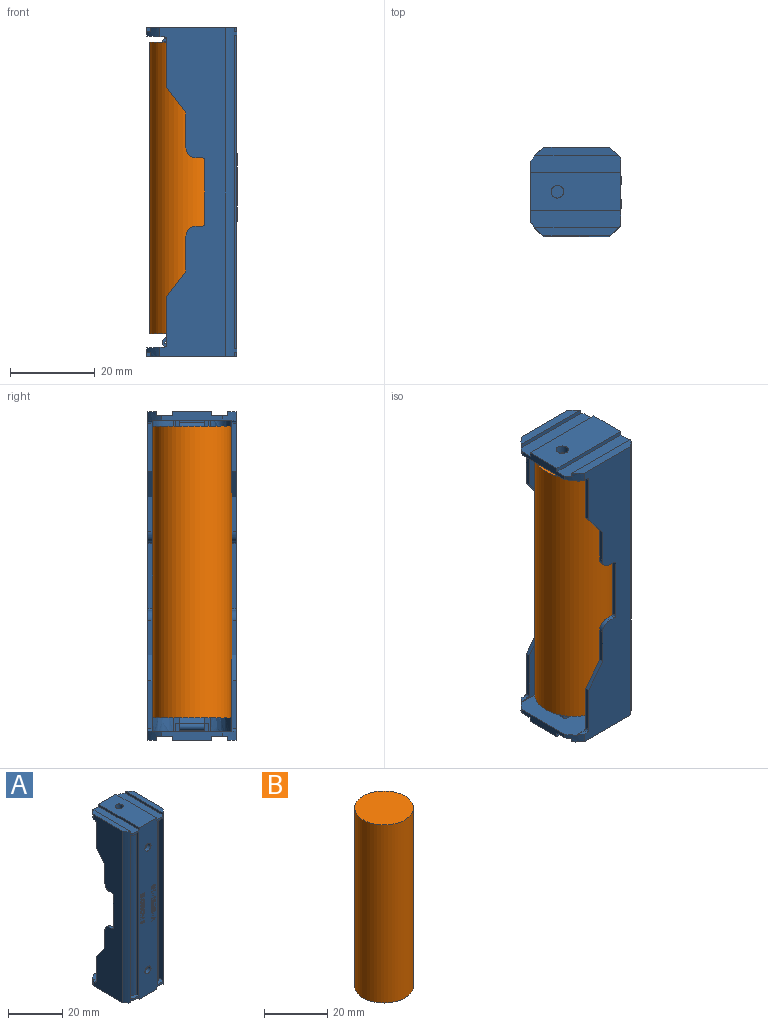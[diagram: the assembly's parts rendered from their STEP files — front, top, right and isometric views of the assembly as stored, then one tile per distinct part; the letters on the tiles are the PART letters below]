
ASSEMBLY  parts=2 mates=1
PART A: 400 faces, bbox 22.9x23.4x83.1 mm
  f0: plane 77.7x15.49mm, normal (0,-1,0), area 740.8mm2, adj f18,f19,f22,f24,f26,f27,f29,f30
  f1: plane 14.29x2mm, normal (0,1,0), area 23.3mm2, adj f5,f22,f24,f32,f120,f121,f396,f397
  f2: plane 19.76x2mm, normal (0,0,-1), area 35.5mm2, adj f9,f23,f394,f396
  f3: plane 19.76x2mm, normal (0,0,-1), area 35.5mm2, adj f10,f21,f395,f397
  f4: plane 19.3x18.9mm, normal (0,0,-1), area 320.5mm2, adj f6,f8,f11,f31,f35,f72,f73,f107
  f5: plane 19.3x18.9mm, normal (0,0,1), area 320.5mm2, adj f1,f7,f12,f31,f38,f72,f73,f96
  f6: plane 28.81x10.37mm, normal (1,0,0), area 156.1mm2, adj f4,f13,f42,f43,f44,f45,f46,f47
  f7: plane 28.81x10.37mm, normal (-1,0,0), area 156.1mm2, adj f5,f15,f57,f58,f59,f60,f61,f62
  f8: plane 14.29x2mm, normal (0,1,0), area 23.3mm2, adj f4,f18,f19,f33,f117,f118,f398,f399
  f9: plane 77.7x15.47mm, normal (1,0,0), area 815.6mm2, adj f2,f15,f16,f41,f57,f58,f59,f60
  f10: plane 77.7x15.47mm, normal (-1,0,0), area 815.6mm2, adj f3,f13,f14,f34,f42,f43,f44,f45
  f11: plane 28.81x10.37mm, normal (-1,0,0), area 156.1mm2, adj f4,f16,f66,f67,f68,f69,f70,f71
  f12: plane 28.81x10.37mm, normal (1,0,0), area 156.1mm2, adj f5,f14,f51,f52,f53,f54,f55,f56
  f13: plane 2.19x1mm, normal (0,0,-1), area 1.6mm2, adj f6,f10,f42,f399
  f14: plane 2.19x1mm, normal (0,0,1), area 1.6mm2, adj f10,f12,f56,f397
  f15: plane 2.19x1mm, normal (0,0,1), area 1.6mm2, adj f7,f9,f57,f396
  f16: plane 2.19x1mm, normal (0,0,-1), area 1.6mm2, adj f9,f11,f71,f398
  f17: plane 19.76x1mm, normal (1,0,0), area 19.8mm2, adj f18,f34,f395,f399
  f18: plane 21.3x3.95mm, normal (0,0,1), area 83.3mm2, adj f0,f8,f17,f117,f395,f399
  f19: plane 21.3x3.95mm, normal (0,0,1), area 83.3mm2, adj f0,f8,f20,f118,f394,f398
  f20: plane 19.76x1mm, normal (-1,0,0), area 19.8mm2, adj f19,f41,f394,f398
  f21: plane 19.76x1mm, normal (1,0,0), area 19.8mm2, adj f3,f22,f395,f397
  f22: plane 21.3x3.95mm, normal (0,0,-1), area 83.3mm2, adj f0,f1,f21,f120,f395,f397
  f23: plane 19.76x1mm, normal (-1,0,0), area 19.8mm2, adj f2,f24,f394,f396
  f24: plane 21.3x3.95mm, normal (0,0,-1), area 83.3mm2, adj f0,f1,f23,f121,f394,f396
  f25: plane 74x2.46mm, normal (1,0,0), area 181.8mm2, adj f26,f27,f123,f395
  f26: plane 3.72x3.24mm, normal (0,0,-1), area 5.8mm2, adj f0,f25,f122,f123,f395
  f27: plane 3.71x3.23mm, normal (0,0,1), area 5.8mm2, adj f0,f25,f122,f123,f395
  f28: plane 74x2.46mm, normal (-1,0,0), area 181.8mm2, adj f29,f30,f125,f394
  f29: plane 3.72x3.24mm, normal (0,0,-1), area 5.8mm2, adj f0,f28,f124,f125,f394
  f30: plane 3.71x3.23mm, normal (0,0,1), area 5.8mm2, adj f0,f28,f124,f125,f394
  f31: plane 73.7x8.9mm, normal (0,1,0), area 572.8mm2, adj f4,f5,f36,f39,f72,f73,f97,f98
  f32: plane 21.3x9mm, normal (0,0,-1), area 184.6mm2, adj f0,f1,f119,f120,f121
  f33: plane 21.3x9mm, normal (0,0,1), area 184.6mm2, adj f0,f8,f116,f117,f118
  f34: plane 19.76x2mm, normal (0,0,1), area 35.5mm2, adj f10,f17,f395,f399
  f35: plane 6x0.58mm, normal (0,1,0), area 3.4mm2, adj f4,f74,f107,f112
  f36: plane 14.74x6mm, normal (0,0,-1), area 79.4mm2, adj f31,f37,f75,f76,f106,f108,f111,f113
  f37: plane 9.57x5.89mm, normal (-1,0,0), area 10.8mm2, adj f36,f74,f76,f77,f78,f79,f80,f81
  f38: plane 6x0.34mm, normal (0,1,0), area 2mm2, adj f5,f85,f96,f101
  f39: plane 14.74x6mm, normal (0,0,1), area 79.4mm2, adj f31,f40,f86,f95,f99,f100,f104,f105
  f40: plane 9.57x5.89mm, normal (1,0,0), area 10.8mm2, adj f39,f85,f87,f88,f89,f90,f91,f92
  f41: plane 19.76x2mm, normal (0,0,1), area 35.5mm2, adj f9,f20,f394,f398
  f42: cylinder r=0.56mm len=1mm, axis (1,0,0), area 0.9mm2, adj f6,f10,f13,f43
  f43: plane 11.35x1mm, normal (0,1,0), area 11.4mm2, adj f6,f10,f42,f44
  f44: plane 6.08x4.59mm, normal (0,0.8,-0.6), area 7.6mm2, adj f6,f10,f43,f45
  f45: plane 8.25x1mm, normal (0,1,0), area 8.2mm2, adj f6,f10,f44,f46
  f46: cylinder r=2.38mm len=2.38mm, axis (1,0,0), area 3.7mm2, adj f6,f10,f45,f47
  f47: plane 1.56x1.05mm, normal (0,0,-1), area 1.6mm2, adj f6,f10,f46,f48,f73
  f48: cylinder r=0.46mm len=1.1mm, axis (1,0,0), area 0.8mm2, adj f10,f47,f49,f73
  f49: plane 15.17x1.1mm, normal (0,1,0), area 16.6mm2, adj f10,f48,f50,f73
  f50: cylinder r=0.46mm len=1.1mm, axis (1,0,0), area 0.8mm2, adj f10,f49,f51,f73
  f51: plane 1.56x1.05mm, normal (0,0,1), area 1.6mm2, adj f10,f12,f50,f52,f73
  f52: cylinder r=2.38mm len=2.38mm, axis (1,0,0), area 3.7mm2, adj f10,f12,f51,f53
  f53: plane 8.25x1mm, normal (0,1,0), area 8.2mm2, adj f10,f12,f52,f54
  f54: plane 6.08x4.59mm, normal (0,0.8,0.6), area 7.6mm2, adj f10,f12,f53,f55
  f55: plane 11.35x1mm, normal (0,1,0), area 11.4mm2, adj f10,f12,f54,f56
  f56: cylinder r=0.56mm len=1mm, axis (1,0,0), area 0.9mm2, adj f10,f12,f14,f55
  f57: cylinder r=0.56mm len=1mm, axis (1,0,0), area 0.9mm2, adj f7,f9,f15,f58
  f58: plane 11.35x1mm, normal (0,1,0), area 11.4mm2, adj f7,f9,f57,f59
  f59: plane 6.08x4.59mm, normal (0,0.8,0.6), area 7.6mm2, adj f7,f9,f58,f60
  f60: plane 8.25x1mm, normal (0,1,0), area 8.2mm2, adj f7,f9,f59,f61
  f61: cylinder r=2.38mm len=2.38mm, axis (1,0,0), area 3.7mm2, adj f7,f9,f60,f62
  f62: plane 1.56x1.05mm, normal (0,0,1), area 1.6mm2, adj f7,f9,f61,f63,f72
  f63: cylinder r=0.46mm len=1.1mm, axis (1,0,0), area 0.8mm2, adj f9,f62,f64,f72
  f64: plane 15.17x1.1mm, normal (0,1,0), area 16.6mm2, adj f9,f63,f65,f72
  f65: cylinder r=0.46mm len=1.1mm, axis (1,0,0), area 0.8mm2, adj f9,f64,f66,f72
  f66: plane 1.56x1.05mm, normal (0,0,-1), area 1.6mm2, adj f9,f11,f65,f67,f72
  f67: cylinder r=2.38mm len=2.38mm, axis (1,0,0), area 3.7mm2, adj f9,f11,f66,f68
  f68: plane 8.25x1mm, normal (0,1,0), area 8.2mm2, adj f9,f11,f67,f69
  f69: plane 6.08x4.59mm, normal (0,0.8,-0.6), area 7.6mm2, adj f9,f11,f68,f70
  f70: plane 11.35x1mm, normal (0,1,0), area 11.4mm2, adj f9,f11,f69,f71
  f71: cylinder r=0.56mm len=1mm, axis (1,0,0), area 0.9mm2, adj f9,f11,f16,f70
  f72: extruded ~73.7x7mm, area 677.7mm2, adj f4,f5,f7,f11,f31,f62,f63,f64
  f73: extruded ~73.7x7mm, area 677.7mm2, adj f4,f5,f6,f12,f31,f47,f48,f49
  f74: plane 14.74x6mm, normal (0,0,1), area 88.4mm2, adj f35,f37,f75,f84,f107,f112
  f75: plane 9.57x5.89mm, normal (1,0,0), area 10.8mm2, adj f36,f74,f76,f77,f78,f79,f80,f81
  f76: cylinder r=0.31mm len=6mm, axis (-1,0,0), area 4.3mm2, adj f36,f37,f75,f77
  f77: plane 6x3.97mm, normal (0,-0.71,0.7), area 33.5mm2, adj f37,f75,f76,f78
  f78: cylinder r=0.67mm len=6mm, axis (-1,0,0), area 3.2mm2, adj f37,f75,f77,f79
  f79: plane 6x4.49mm, normal (0,0,1), area 26.9mm2, adj f37,f75,f78,f80
  f80: plane 6x0.6mm, normal (0,-1,0), area 3.6mm2, adj f37,f75,f79,f81
  f81: plane 6x4.49mm, normal (0,0,-1), area 26.9mm2, adj f37,f75,f80,f82
  f82: cylinder r=1.27mm len=6mm, axis (-1,0,0), area 6mm2, adj f37,f75,f81,f83
  f83: plane 6x3.97mm, normal (0,0.71,-0.7), area 33.5mm2, adj f37,f75,f82,f84
  f84: cylinder r=0.91mm len=6mm, axis (-1,0,0), area 12.8mm2, adj f37,f74,f75,f83
  f85: plane 14.74x6mm, normal (0,0,-1), area 88.4mm2, adj f38,f40,f86,f87,f96,f101
  f86: plane 9.57x5.89mm, normal (-1,0,0), area 10.8mm2, adj f39,f85,f87,f88,f89,f90,f91,f92
  f87: cylinder r=0.91mm len=6mm, axis (-1,0,0), area 12.8mm2, adj f40,f85,f86,f88
  f88: plane 6x3.97mm, normal (0,0.71,0.7), area 33.5mm2, adj f40,f86,f87,f89
  f89: cylinder r=1.27mm len=6mm, axis (-1,0,0), area 6mm2, adj f40,f86,f88,f90
  f90: plane 6x4.49mm, normal (0,0,1), area 26.9mm2, adj f40,f86,f89,f91
  f91: plane 6x0.6mm, normal (0,-1,0), area 3.6mm2, adj f40,f86,f90,f92
  f92: plane 6x4.49mm, normal (0,0,-1), area 26.9mm2, adj f40,f86,f91,f93
  f93: cylinder r=0.67mm len=6mm, axis (-1,0,0), area 3.2mm2, adj f40,f86,f92,f94
  f94: plane 6x3.97mm, normal (0,-0.71,-0.7), area 33.5mm2, adj f40,f86,f93,f95
  f95: cylinder r=0.31mm len=6mm, axis (-1,0,0), area 4.3mm2, adj f39,f40,f86,f94
  f96: plane 9x0.34mm, normal (1,0,0), area 3.1mm2, adj f5,f38,f85,f100
  f97: plane 9x1.94mm, normal (-1,0,0), area 17.5mm2, adj f5,f31,f98,f100
  f98: plane 9x1.5mm, normal (0,0,1), area 13.5mm2, adj f31,f97,f99,f100
  f99: plane 9x1mm, normal (1,0,0), area 9mm2, adj f31,f39,f98,f100
  f100: plane 1.94x1.5mm, normal (0,1,0), area 2.4mm2, adj f5,f39,f86,f96,f97,f98,f99
  f101: plane 9x0.34mm, normal (-1,0,0), area 3.1mm2, adj f5,f38,f85,f105
  f102: plane 9x1.5mm, normal (0,0,1), area 13.5mm2, adj f31,f103,f104,f105
  f103: plane 9x1.94mm, normal (1,0,0), area 17.5mm2, adj f5,f31,f102,f105
  f104: plane 9x1mm, normal (-1,0,0), area 9mm2, adj f31,f39,f102,f105
  f105: plane 1.94x1.5mm, normal (0,1,0), area 2.4mm2, adj f5,f39,f40,f101,f102,f103,f104
  f106: plane 9x0.76mm, normal (-1,0,0), area 6.9mm2, adj f31,f36,f108,f110
  f107: plane 9x0.58mm, normal (-1,0,0), area 5.2mm2, adj f4,f35,f74,f108
  f108: plane 1.94x1.5mm, normal (0,1,0), area 2.3mm2, adj f4,f36,f75,f106,f107,f109,f110
  f109: plane 9x1.94mm, normal (1,0,0), area 17.5mm2, adj f4,f31,f108,f110
  f110: plane 9x1.5mm, normal (0,0,-1), area 13.5mm2, adj f31,f106,f108,f109
  f111: plane 9x0.76mm, normal (1,0,0), area 6.9mm2, adj f31,f36,f113,f114
  f112: plane 9x0.58mm, normal (1,0,0), area 5.2mm2, adj f4,f35,f74,f113
  f113: plane 1.94x1.5mm, normal (0,1,0), area 2.3mm2, adj f4,f36,f37,f111,f112,f114,f115
  f114: plane 9x1.5mm, normal (0,0,-1), area 13.5mm2, adj f31,f111,f113,f115
  f115: plane 9x1.94mm, normal (-1,0,0), area 17.5mm2, adj f4,f31,f113,f114
  f116: cylinder r=1.5mm len=3mm, axis (0,0,1), area 18.8mm2, adj f4,f33
  f117: plane 21.3x1mm, normal (-1,0,0), area 21.3mm2, adj f0,f8,f18,f33
  f118: plane 21.3x1mm, normal (1,0,0), area 21.3mm2, adj f0,f8,f19,f33
  f119: cylinder r=1.5mm len=3mm, axis (0,0,-1), area 18.8mm2, adj f5,f32
  f120: plane 21.3x1mm, normal (-1,0,0), area 21.3mm2, adj f0,f1,f22,f32
  f121: plane 21.3x1mm, normal (1,0,0), area 21.3mm2, adj f0,f1,f24,f32
  f122: plane 74x1.03mm, normal (-1,0,0), area 76mm2, adj f0,f26,f27,f123
  f123: offset ~83.07x9mm, area 305.4mm2, adj f25,f26,f27,f122
  f124: plane 74x1.03mm, normal (1,0,0), area 76mm2, adj f0,f29,f30,f125
  f125: offset ~83.07x9mm, area 305.4mm2, adj f28,f29,f30,f124
  f126: cylinder r=1.6mm len=3.2mm, axis (0,1,0), area 18.1mm2, adj f0,f127
  f127: plane 5.08x5.08mm, normal (0,1,0), area 12.2mm2, adj f126,f128
  f128: cylinder r=2.54mm len=5.08mm, axis (0,1,0), area 3.2mm2, adj f31,f127
  f129: cylinder r=1.6mm len=3.2mm, axis (0,1,0), area 18.1mm2, adj f0,f130
  f130: plane 5.08x5.08mm, normal (0,1,0), area 12.2mm2, adj f129,f131
  f131: cylinder r=2.54mm len=5.08mm, axis (0,1,0), area 3.2mm2, adj f31,f130
  f132: plane 1.8x1.06mm, normal (0,-1,0), area 0.9mm2, adj f133,f134,f135,f136,f137,f138,f139,f140
  f133: plane 1.8x0.1mm, normal (0,0,1), area 0.2mm2, adj f0,f132,f134,f139
  f134: plane 0.49x0.1mm, normal (-1,0,0), area 0mm2, adj f0,f132,f133,f135
  f135: extruded ~0.57x0.51mm, area 0.1mm2, adj f0,f132,f134,f136
  f136: extruded ~0.46x0.35mm, area 0.1mm2, adj f0,f132,f135,f137
  f137: extruded ~0.38x0.21mm, area 0mm2, adj f0,f132,f136,f138
  f138: extruded ~0.57x0.45mm, area 0.1mm2, adj f0,f132,f137,f139
  f139: plane 0.35x0.1mm, normal (1,0,0), area 0mm2, adj f0,f132,f133,f138
  f140: plane 0.22x0.1mm, normal (-1,0,0), area 0mm2, adj f132,f141,f144,f152
  f141: plane 0.58x0.1mm, normal (0,0,-1), area 0.1mm2, adj f132,f140,f142,f152
  f142: plane 0.11x0.1mm, normal (1,0,0), area 0mm2, adj f132,f141,f143,f152
  f143: extruded ~0.49x0.31mm, area 0.1mm2, adj f132,f142,f144,f152
  f144: extruded ~0.38x0.26mm, area 0.1mm2, adj f132,f140,f143,f152
  f145: plane 0.11x0.1mm, normal (-1,0,0), area 0mm2, adj f132,f146,f150,f151
  f146: plane 0.67x0.1mm, normal (0,0,-1), area 0.1mm2, adj f132,f145,f147,f151
  f147: plane 0.23x0.1mm, normal (1,0,0), area 0mm2, adj f132,f146,f148,f151
  f148: extruded ~0.51x0.33mm, area 0.1mm2, adj f132,f147,f149,f151
  f149: extruded ~0.32x0.29mm, area 0mm2, adj f132,f148,f150,f151
  f150: extruded ~0.34x0.1mm, area 0mm2, adj f132,f145,f149,f151
  f151: plane 0.74x0.67mm, normal (0,-1,0), area 0.4mm2, adj f145,f146,f147,f148,f149,f150
  f152: plane 0.6x0.58mm, normal (0,-1,0), area 0.3mm2, adj f140,f141,f142,f143,f144
  f153: plane 1.8x0.1mm, normal (0,0,1), area 0.2mm2, adj f0,f154,f164,f165
  f154: plane 0.16x0.1mm, normal (-1,0,0), area 0mm2, adj f0,f153,f155,f165
  f155: plane 0.88x0.1mm, normal (0,0,-1), area 0.1mm2, adj f0,f154,f156,f165
  f156: plane 0.92x0.1mm, normal (-1,0,0), area 0.1mm2, adj f0,f155,f157,f165
  f157: plane 0.88x0.1mm, normal (0,0,1), area 0.1mm2, adj f0,f156,f158,f165
  f158: plane 0.16x0.1mm, normal (-1,0,0), area 0mm2, adj f0,f157,f159,f165
  f159: plane 1.8x0.1mm, normal (0,0,-1), area 0.2mm2, adj f0,f158,f160,f165
  f160: plane 0.16x0.1mm, normal (1,0,0), area 0mm2, adj f0,f159,f161,f165
  f161: plane 0.74x0.1mm, normal (0,0,1), area 0.1mm2, adj f0,f160,f162,f165
  f162: plane 0.92x0.1mm, normal (1,0,0), area 0.1mm2, adj f0,f161,f163,f165
  f163: plane 0.74x0.1mm, normal (0,0,-1), area 0.1mm2, adj f0,f162,f164,f165
  f164: plane 0.16x0.1mm, normal (1,0,0), area 0mm2, adj f0,f153,f163,f165
  f165: plane 1.8x1.25mm, normal (0,-1,0), area 0.8mm2, adj f153,f154,f155,f156,f157,f158,f159,f160
  f166: plane 0.18x0.1mm, normal (0,0,1), area 0mm2, adj f0,f167,f169,f170
  f167: plane 0.69x0.1mm, normal (-1,0,0), area 0.1mm2, adj f0,f166,f168,f170
  f168: plane 0.18x0.1mm, normal (0,0,-1), area 0mm2, adj f0,f167,f169,f170
  f169: plane 0.69x0.1mm, normal (1,0,0), area 0.1mm2, adj f0,f166,f168,f170
  f170: plane 0.69x0.18mm, normal (0,-1,0), area 0.1mm2, adj f166,f167,f168,f169
  f171: plane 0.18x0.11mm, normal (0.5,0,0.87), area 0mm2, adj f0,f172,f176,f177
  f172: plane 0.28x0.1mm, normal (-1,0,0), area 0mm2, adj f0,f171,f173,f177
  f173: plane 1.62x0.1mm, normal (0,0,1), area 0.2mm2, adj f0,f172,f174,f177
  f174: plane 0.16x0.1mm, normal (-1,0,0), area 0mm2, adj f0,f173,f175,f177
  f175: plane 1.8x0.1mm, normal (0,0,-1), area 0.2mm2, adj f0,f174,f176,f177
  f176: plane 0.33x0.1mm, normal (1,0,0), area 0mm2, adj f0,f171,f175,f177
  f177: plane 1.8x0.44mm, normal (0,-1,0), area 0.3mm2, adj f171,f172,f173,f174,f175,f176
  f178: plane 1.89x1.22mm, normal (0,-1,0), area 0.9mm2, adj f179,f180,f181,f182,f183,f184,f185,f186
  f179: extruded ~0.38x0.26mm, area 0mm2, adj f0,f178,f180,f187
  f180: extruded ~0.51x0.47mm, area 0.1mm2, adj f0,f178,f179,f181
  f181: extruded ~0.53x0.46mm, area 0.1mm2, adj f0,f178,f180,f182
  f182: extruded ~0.38x0.26mm, area 0mm2, adj f0,f178,f181,f183
  f183: extruded ~0.49x0.36mm, area 0.1mm2, adj f0,f178,f182,f184
  f184: extruded ~0.61x0.56mm, area 0.1mm2, adj f0,f178,f183,f185
  f185: extruded ~0.48x0.2mm, area 0.1mm2, adj f0,f178,f184,f186
  f186: cylinder r=0.57mm len=0.37mm, axis (0,1,0), area 0mm2, adj f0,f178,f185,f187
  f187: extruded ~0.48x0.35mm, area 0.1mm2, adj f0,f178,f179,f186
  f188: extruded ~0.36x0.28mm, area 0.1mm2, adj f178,f189,f191,f197
  f189: extruded ~0.36x0.28mm, area 0.1mm2, adj f178,f188,f190,f197
  f190: extruded ~0.36x0.3mm, area 0.1mm2, adj f178,f189,f191,f197
  f191: extruded ~0.35x0.3mm, area 0.1mm2, adj f178,f188,f190,f197
  f192: extruded ~0.44x0.38mm, area 0.1mm2, adj f178,f193,f195,f196
  f193: extruded ~0.46x0.4mm, area 0.1mm2, adj f178,f192,f194,f196
  f194: extruded ~0.45x0.37mm, area 0.1mm2, adj f178,f193,f195,f196
  f195: extruded ~0.45x0.38mm, area 0.1mm2, adj f178,f192,f194,f196
  f196: plane 0.9x0.76mm, normal (0,-1,0), area 0.5mm2, adj f192,f193,f194,f195
  f197: plane 0.72x0.58mm, normal (0,-1,0), area 0.3mm2, adj f188,f189,f190,f191
  f198: plane 1.89x1.11mm, normal (0,-1,0), area 0.7mm2, adj f199,f200,f201,f202,f203,f204,f205,f206
  f199: plane 0.82x0.54mm, normal (0.55,0,0.84), area 0.1mm2, adj f0,f198,f200,f206
  f200: extruded ~0.52x0.2mm, area 0.1mm2, adj f0,f198,f199,f201
  f201: extruded ~0.55x0.55mm, area 0.1mm2, adj f0,f198,f200,f202
  f202: extruded ~0.56x0.55mm, area 0.1mm2, adj f0,f198,f201,f203
  f203: extruded ~0.53x0.53mm, area 0.1mm2, adj f0,f198,f202,f204
  f204: cylinder r=1.13mm len=0.19mm, axis (0,1,0), area 0mm2, adj f0,f198,f203,f205
  f205: plane 0.73x0.48mm, normal (-0.55,0,-0.84), area 0.1mm2, adj f0,f198,f204,f206
  f206: plane 0.12x0.1mm, normal (0.79,0,-0.62), area 0mm2, adj f0,f198,f199,f205
  f207: extruded ~0.41x0.36mm, area 0.1mm2, adj f198,f208,f210,f211
  f208: extruded ~0.38x0.36mm, area 0.1mm2, adj f198,f207,f209,f211
  f209: extruded ~0.39x0.36mm, area 0.1mm2, adj f198,f208,f210,f211
  f210: extruded ~0.39x0.36mm, area 0.1mm2, adj f198,f207,f209,f211
  f211: plane 0.78x0.72mm, normal (0,-1,0), area 0.4mm2, adj f207,f208,f209,f210
  f212: plane 0.74x0.1mm, normal (1,0,0), area 0.1mm2, adj f0,f213,f225,f226
  f213: plane 0.9x0.18mm, normal (0.2,0,0.98), area 0.1mm2, adj f0,f212,f214,f226
  f214: extruded ~0.4x0.1mm, area 0mm2, adj f0,f213,f215,f226
  f215: extruded ~0.43x0.4mm, area 0.1mm2, adj f0,f214,f216,f226
  f216: cylinder r=0.45mm len=0.46mm, axis (0,-1,0), area 0.1mm2, adj f0,f215,f217,f226
  f217: extruded ~0.4x0.32mm, area 0.1mm2, adj f0,f216,f218,f226
  f218: plane 0.16x0.1mm, normal (1,0,0), area 0mm2, adj f0,f217,f219,f226
  f219: extruded ~0.55x0.51mm, area 0.1mm2, adj f0,f218,f220,f226
  f220: extruded ~0.63x0.63mm, area 0.1mm2, adj f0,f219,f221,f226
  f221: extruded ~0.59x0.57mm, area 0.1mm2, adj f0,f220,f222,f226
  f222: cylinder r=0.76mm len=0.21mm, axis (0,1,0), area 0mm2, adj f0,f221,f223,f226
  f223: plane 0.47x0.1mm, normal (-0.2,0,-0.98), area 0mm2, adj f0,f222,f224,f226
  f224: plane 0.61x0.1mm, normal (-1,0,0), area 0.1mm2, adj f0,f223,f225,f226
  f225: plane 0.18x0.1mm, normal (0,0,-1), area 0mm2, adj f0,f212,f224,f226
  f226: plane 1.85x1.18mm, normal (0,-1,0), area 0.7mm2, adj f212,f213,f214,f215,f216,f217,f218,f219
  f227: plane 1.89x1.22mm, normal (0,-1,0), area 0.8mm2, adj f228,f229,f230,f231,f232,f233,f234,f235
  f228: extruded ~0.95x0.6mm, area 0.1mm2, adj f0,f227,f229,f231
  f229: extruded ~0.95x0.62mm, area 0.1mm2, adj f0,f227,f228,f230
  f230: extruded ~0.95x0.62mm, area 0.1mm2, adj f0,f227,f229,f231
  f231: extruded ~0.95x0.6mm, area 0.1mm2, adj f0,f227,f228,f230
  f232: extruded ~0.76x0.45mm, area 0.1mm2, adj f227,f233,f236,f237
  f233: extruded ~0.76x0.45mm, area 0.1mm2, adj f227,f232,f234,f237
  f234: extruded ~0.39x0.31mm, area 0.1mm2, adj f227,f233,f235,f237
  f235: extruded ~0.45x0.1mm, area 0mm2, adj f227,f234,f236,f237
  f236: extruded ~0.76x0.45mm, area 0.1mm2, adj f227,f232,f235,f237
  f237: plane 1.52x0.9mm, normal (0,-1,0), area 1.1mm2, adj f232,f233,f234,f235,f236
  f238: plane 0.18x0.1mm, normal (0,0,1), area 0mm2, adj f0,f239,f241,f242
  f239: plane 0.69x0.1mm, normal (-1,0,0), area 0.1mm2, adj f0,f238,f240,f242
  f240: plane 0.18x0.1mm, normal (0,0,-1), area 0mm2, adj f0,f239,f241,f242
  f241: plane 0.69x0.1mm, normal (1,0,0), area 0.1mm2, adj f0,f238,f240,f242
  f242: plane 0.69x0.18mm, normal (0,-1,0), area 0.1mm2, adj f238,f239,f240,f241
  f243: plane 1.8x1.71mm, normal (0,-1,0), area 0.7mm2, adj f244,f245,f246,f247,f248,f249,f250,f251
  f244: plane 0.1x0.02mm, normal (1,0,0), area 0mm2, adj f0,f243,f245,f251
  f245: plane 1.8x0.85mm, normal (0.43,0,0.9), area 0.2mm2, adj f0,f243,f244,f246
  f246: plane 0.18x0.1mm, normal (-1,0,0), area 0mm2, adj f0,f243,f245,f247
  f247: plane 0.58x0.27mm, normal (-0.43,0,-0.9), area 0.1mm2, adj f0,f243,f246,f248
  f248: plane 0.82x0.1mm, normal (-1,0,0), area 0.1mm2, adj f0,f243,f247,f249
  f249: plane 0.58x0.27mm, normal (-0.42,0,0.91), area 0.1mm2, adj f0,f243,f248,f250
  f250: plane 0.18x0.1mm, normal (-1,0,0), area 0mm2, adj f0,f243,f249,f251
  f251: plane 1.8x0.83mm, normal (0.42,0,-0.91), area 0.2mm2, adj f0,f243,f244,f250
  f252: plane 0.69x0.32mm, normal (-0.42,0,0.91), area 0.1mm2, adj f243,f253,f254,f255
  f253: plane 0.69x0.33mm, normal (-0.43,0,-0.9), area 0.1mm2, adj f243,f252,f254,f255
  f254: plane 0.64x0.1mm, normal (1,0,0), area 0.1mm2, adj f243,f252,f253,f255
  f255: plane 0.69x0.64mm, normal (0,-1,0), area 0.2mm2, adj f252,f253,f254
  f256: plane 1.8x1.06mm, normal (0,-1,0), area 0.9mm2, adj f257,f258,f259,f260,f261,f262,f263,f264
  f257: plane 1.8x0.1mm, normal (0,0,1), area 0.2mm2, adj f0,f256,f258,f263
  f258: plane 0.49x0.1mm, normal (-1,0,0), area 0mm2, adj f0,f256,f257,f259
  f259: extruded ~0.57x0.51mm, area 0.1mm2, adj f0,f256,f258,f260
  f260: extruded ~0.46x0.35mm, area 0.1mm2, adj f0,f256,f259,f261
  f261: extruded ~0.38x0.21mm, area 0mm2, adj f0,f256,f260,f262
  f262: extruded ~0.57x0.45mm, area 0.1mm2, adj f0,f256,f261,f263
  f263: plane 0.35x0.1mm, normal (1,0,0), area 0mm2, adj f0,f256,f257,f262
  f264: plane 0.22x0.1mm, normal (-1,0,0), area 0mm2, adj f256,f265,f268,f276
  f265: plane 0.58x0.1mm, normal (0,0,-1), area 0.1mm2, adj f256,f264,f266,f276
  f266: plane 0.11x0.1mm, normal (1,0,0), area 0mm2, adj f256,f265,f267,f276
  f267: extruded ~0.49x0.31mm, area 0.1mm2, adj f256,f266,f268,f276
  f268: extruded ~0.38x0.26mm, area 0.1mm2, adj f256,f264,f267,f276
  f269: plane 0.11x0.1mm, normal (-1,0,0), area 0mm2, adj f256,f270,f274,f275
  f270: plane 0.67x0.1mm, normal (0,0,-1), area 0.1mm2, adj f256,f269,f271,f275
  f271: plane 0.23x0.1mm, normal (1,0,0), area 0mm2, adj f256,f270,f272,f275
  f272: extruded ~0.51x0.33mm, area 0.1mm2, adj f256,f271,f273,f275
  f273: extruded ~0.32x0.29mm, area 0mm2, adj f256,f272,f274,f275
  f274: extruded ~0.34x0.1mm, area 0mm2, adj f256,f269,f273,f275
  f275: plane 0.74x0.67mm, normal (0,-1,0), area 0.4mm2, adj f269,f270,f271,f272,f273,f274
  f276: plane 0.6x0.58mm, normal (0,-1,0), area 0.3mm2, adj f264,f265,f266,f267,f268
  f277: plane 1.8x0.1mm, normal (0,0,1), area 0.2mm2, adj f0,f278,f282,f283
  f278: plane 0.85x0.1mm, normal (-1,0,0), area 0.1mm2, adj f0,f277,f279,f283
  f279: plane 0.18x0.1mm, normal (0,0,-1), area 0mm2, adj f0,f278,f280,f283
  f280: plane 0.69x0.1mm, normal (1,0,0), area 0.1mm2, adj f0,f279,f281,f283
  f281: plane 1.62x0.1mm, normal (0,0,-1), area 0.2mm2, adj f0,f280,f282,f283
  f282: plane 0.16x0.1mm, normal (1,0,0), area 0mm2, adj f0,f277,f281,f283
  f283: plane 1.8x0.85mm, normal (0,-1,0), area 0.4mm2, adj f277,f278,f279,f280,f281,f282
  f284: plane 1.89x1.89mm, normal (0,-1,0), area 0.9mm2, adj f285,f286,f287,f288,f289,f290,f291,f292
  f285: extruded ~0.95x0.93mm, area 0.1mm2, adj f0,f284,f286,f288
  f286: extruded ~0.95x0.94mm, area 0.1mm2, adj f0,f284,f285,f287
  f287: extruded ~0.95x0.94mm, area 0.1mm2, adj f0,f284,f286,f288
  f288: extruded ~0.96x0.95mm, area 0.2mm2, adj f0,f284,f285,f287
  f289: extruded ~0.79x0.76mm, area 0.1mm2, adj f284,f290,f292,f293
  f290: extruded ~0.78x0.77mm, area 0.1mm2, adj f284,f289,f291,f293
  f291: extruded ~0.78x0.75mm, area 0.1mm2, adj f284,f290,f292,f293
  f292: extruded ~0.79x0.76mm, area 0.1mm2, adj f284,f289,f291,f293
  f293: plane 1.57x1.52mm, normal (0,-1,0), area 1.9mm2, adj f289,f290,f291,f292
  f294: extruded ~0.55x0.39mm, area 0.1mm2, adj f0,f295,f310,f311
  f295: extruded ~0.51x0.49mm, area 0.1mm2, adj f0,f294,f296,f311
  f296: extruded ~0.58x0.42mm, area 0.1mm2, adj f0,f295,f297,f311
  f297: cylinder r=3.85mm len=0.24mm, axis (0,-1,0), area 0mm2, adj f0,f296,f298,f311
  f298: extruded ~0.23x0.12mm, area 0mm2, adj f0,f297,f299,f311
  f299: extruded ~0.26x0.23mm, area 0mm2, adj f0,f298,f300,f311
  f300: extruded ~0.35x0.23mm, area 0mm2, adj f0,f299,f301,f311
  f301: plane 0.15x0.11mm, normal (-0.8,0,-0.6), area 0mm2, adj f0,f300,f302,f311
  f302: extruded ~0.48x0.3mm, area 0.1mm2, adj f0,f301,f303,f311
  f303: extruded ~0.44x0.42mm, area 0.1mm2, adj f0,f302,f304,f311
  f304: cylinder r=0.43mm len=0.27mm, axis (0,1,0), area 0mm2, adj f0,f303,f305,f311
  f305: extruded ~0.3x0.25mm, area 0mm2, adj f0,f304,f306,f311
  f306: extruded ~0.32x0.29mm, area 0mm2, adj f0,f305,f307,f311
  f307: cylinder r=0.3mm len=0.18mm, axis (0,-1,0), area 0mm2, adj f0,f306,f308,f311
  f308: extruded ~0.35x0.31mm, area 0.1mm2, adj f0,f307,f309,f311
  f309: extruded ~0.4x0.3mm, area 0.1mm2, adj f0,f308,f310,f311
  f310: plane 0.15x0.1mm, normal (0.86,0,0.51), area 0mm2, adj f0,f294,f309,f311
  f311: plane 1.89x1.06mm, normal (0,-1,0), area 0.6mm2, adj f294,f295,f296,f297,f298,f299,f300,f301
  f312: extruded ~0.55x0.39mm, area 0.1mm2, adj f0,f313,f328,f329
  f313: extruded ~0.51x0.49mm, area 0.1mm2, adj f0,f312,f314,f329
  f314: extruded ~0.58x0.42mm, area 0.1mm2, adj f0,f313,f315,f329
  f315: cylinder r=3.85mm len=0.24mm, axis (0,-1,0), area 0mm2, adj f0,f314,f316,f329
  f316: extruded ~0.23x0.12mm, area 0mm2, adj f0,f315,f317,f329
  f317: extruded ~0.26x0.23mm, area 0mm2, adj f0,f316,f318,f329
  f318: extruded ~0.35x0.23mm, area 0mm2, adj f0,f317,f319,f329
  f319: plane 0.15x0.11mm, normal (-0.8,0,-0.6), area 0mm2, adj f0,f318,f320,f329
  f320: extruded ~0.48x0.3mm, area 0.1mm2, adj f0,f319,f321,f329
  f321: extruded ~0.44x0.42mm, area 0.1mm2, adj f0,f320,f322,f329
  f322: cylinder r=0.43mm len=0.27mm, axis (0,1,0), area 0mm2, adj f0,f321,f323,f329
  f323: extruded ~0.3x0.25mm, area 0mm2, adj f0,f322,f324,f329
  f324: extruded ~0.32x0.29mm, area 0mm2, adj f0,f323,f325,f329
  f325: cylinder r=0.3mm len=0.18mm, axis (0,-1,0), area 0mm2, adj f0,f324,f326,f329
  f326: extruded ~0.35x0.31mm, area 0.1mm2, adj f0,f325,f327,f329
  f327: extruded ~0.4x0.3mm, area 0.1mm2, adj f0,f326,f328,f329
  f328: plane 0.15x0.1mm, normal (0.86,0,0.51), area 0mm2, adj f0,f312,f327,f329
  f329: plane 1.89x1.06mm, normal (0,-1,0), area 0.6mm2, adj f312,f313,f314,f315,f316,f317,f318,f319
  f330: plane 1.89x1.89mm, normal (0,-1,0), area 0.9mm2, adj f331,f332,f333,f334,f335,f336,f337,f338
  f331: extruded ~0.95x0.93mm, area 0.1mm2, adj f0,f330,f332,f334
  f332: extruded ~0.95x0.94mm, area 0.1mm2, adj f0,f330,f331,f333
  f333: extruded ~0.95x0.94mm, area 0.1mm2, adj f0,f330,f332,f334
  f334: extruded ~0.96x0.95mm, area 0.2mm2, adj f0,f330,f331,f333
  f335: extruded ~0.79x0.76mm, area 0.1mm2, adj f330,f336,f338,f339
  f336: extruded ~0.78x0.77mm, area 0.1mm2, adj f330,f335,f337,f339
  f337: extruded ~0.78x0.75mm, area 0.1mm2, adj f330,f336,f338,f339
  f338: extruded ~0.79x0.76mm, area 0.1mm2, adj f330,f335,f337,f339
  f339: plane 1.57x1.52mm, normal (0,-1,0), area 1.9mm2, adj f335,f336,f337,f338
  f340: plane 0.16x0.1mm, normal (-1,0,0), area 0mm2, adj f0,f341,f352,f353
  f341: plane 1.3x0.17mm, normal (-0.13,0,-0.99), area 0.1mm2, adj f0,f340,f342,f353
  f342: plane 1.3x0.65mm, normal (-0.45,0,0.89), area 0.1mm2, adj f0,f341,f343,f353
  f343: plane 0.1x0.04mm, normal (-1,0,0), area 0mm2, adj f0,f342,f344,f353
  f344: plane 1.3x0.65mm, normal (-0.45,0,-0.89), area 0.1mm2, adj f0,f343,f345,f353
  f345: plane 1.3x0.17mm, normal (-0.13,0,0.99), area 0.1mm2, adj f0,f344,f346,f353
  f346: plane 0.16x0.1mm, normal (-1,0,0), area 0mm2, adj f0,f345,f347,f353
  f347: plane 1.8x0.24mm, normal (0.13,0,-0.99), area 0.2mm2, adj f0,f346,f348,f353
  f348: plane 0.1x0.02mm, normal (1,0,0), area 0mm2, adj f0,f347,f349,f353
  f349: plane 1.48x0.74mm, normal (0.45,0,0.89), area 0.2mm2, adj f0,f348,f350,f353
  f350: plane 1.48x0.74mm, normal (0.45,0,-0.89), area 0.2mm2, adj f0,f349,f351,f353
  f351: plane 0.1x0.02mm, normal (1,0,0), area 0mm2, adj f0,f350,f352,f353
  f352: plane 1.8x0.24mm, normal (0.13,0,0.99), area 0.2mm2, adj f0,f340,f351,f353
  f353: plane 2.01x1.8mm, normal (0,-1,0), area 1mm2, adj f340,f341,f342,f343,f344,f345,f346,f347
  f354: extruded ~0.38x0.28mm, area 0.1mm2, adj f0,f355,f370,f371
  f355: extruded ~0.36x0.28mm, area 0.1mm2, adj f0,f354,f356,f371
  f356: extruded ~0.46x0.29mm, area 0.1mm2, adj f0,f355,f357,f371
  f357: plane 0.18x0.1mm, normal (0,0,1), area 0mm2, adj f0,f356,f358,f371
  f358: extruded ~0.55x0.38mm, area 0.1mm2, adj f0,f357,f359,f371
  f359: extruded ~0.46x0.38mm, area 0.1mm2, adj f0,f358,f360,f371
  f360: extruded ~0.3x0.1mm, area 0mm2, adj f0,f359,f361,f371
  f361: extruded ~0.25x0.14mm, area 0mm2, adj f0,f360,f362,f371
  f362: plane 0.16x0.1mm, normal (1,0,0), area 0mm2, adj f0,f361,f363,f371
  f363: extruded ~0.6x0.53mm, area 0.1mm2, adj f0,f362,f364,f371
  f364: extruded ~0.62x0.58mm, area 0.1mm2, adj f0,f363,f365,f371
  f365: cylinder r=0.52mm len=0.32mm, axis (0,1,0), area 0mm2, adj f0,f364,f366,f371
  f366: cylinder r=0.49mm len=0.2mm, axis (0,1,0), area 0mm2, adj f0,f365,f367,f371
  f367: extruded ~0.37x0.21mm, area 0mm2, adj f0,f366,f368,f371
  f368: extruded ~0.53x0.47mm, area 0.1mm2, adj f0,f367,f369,f371
  f369: extruded ~0.54x0.46mm, area 0.1mm2, adj f0,f368,f370,f371
  f370: plane 0.16x0.1mm, normal (-1,0,0), area 0mm2, adj f0,f354,f369,f371
  f371: plane 1.89x1.22mm, normal (0,-1,0), area 0.7mm2, adj f354,f355,f356,f357,f358,f359,f360,f361
  f372: plane 2.27x0.1mm, normal (0,0,1), area 0.2mm2, adj f373,f376,f377,f378
  f373: plane 0.8x0.1mm, normal (1,0,0), area 0.1mm2, adj f372,f374,f377,f378
  f374: plane 2.27x0.1mm, normal (0,0,-1), area 0.2mm2, adj f373,f376,f377,f378
  f375: cylinder r=1.8mm len=3.61mm, axis (0,1,0), area 1.1mm2, adj f31,f377
  f376: plane 0.8x0.1mm, normal (-1,0,0), area 0.1mm2, adj f372,f374,f377,f378
  f377: plane 3.61x3.61mm, normal (0,1,0), area 8.4mm2, adj f372,f373,f374,f375,f376
  f378: plane 2.27x0.8mm, normal (0,1,0), area 1.8mm2, adj f372,f373,f374,f376
  f379: plane 0.73x0.1mm, normal (0,0,-1), area 0.1mm2, adj f380,f390,f392,f393
  f380: plane 0.83x0.1mm, normal (1,0,0), area 0.1mm2, adj f379,f381,f392,f393
  f381: plane 0.71x0.1mm, normal (0,0,-1), area 0.1mm2, adj f380,f382,f392,f393
  f382: plane 0.83x0.1mm, normal (-1,0,0), area 0.1mm2, adj f381,f383,f392,f393
  f383: plane 0.83x0.1mm, normal (0,0,-1), area 0.1mm2, adj f382,f384,f392,f393
  f384: plane 0.8x0.1mm, normal (-1,0,0), area 0.1mm2, adj f383,f385,f392,f393
  f385: plane 0.83x0.1mm, normal (0,0,1), area 0.1mm2, adj f384,f386,f392,f393
  f386: plane 0.85x0.1mm, normal (-1,0,0), area 0.1mm2, adj f385,f387,f392,f393
  f387: plane 0.71x0.1mm, normal (0,0,1), area 0.1mm2, adj f386,f388,f392,f393
  f388: plane 0.85x0.1mm, normal (1,0,0), area 0.1mm2, adj f387,f389,f392,f393
  f389: plane 0.73x0.1mm, normal (0,0,1), area 0.1mm2, adj f388,f390,f392,f393
  f390: plane 0.8x0.1mm, normal (1,0,0), area 0.1mm2, adj f379,f389,f392,f393
  f391: cylinder r=1.8mm len=3.61mm, axis (0,1,0), area 1.1mm2, adj f31,f392
  f392: plane 3.61x3.61mm, normal (0,1,0), area 7.2mm2, adj f379,f380,f381,f382,f383,f384,f385,f386
  f393: plane 2.47x2.27mm, normal (0,1,0), area 3mm2, adj f379,f380,f381,f382,f383,f384,f385,f386
  f394: cylinder r=13mm len=77.7mm, axis (0,0,1), area 230mm2, adj f0,f2,f9,f19,f20,f23,f24,f28
  f395: cylinder r=13mm len=77.7mm, axis (0,0,1), area 230mm2, adj f0,f3,f10,f17,f18,f21,f22,f25
  f396: cylinder r=13mm len=3.3mm, axis (0,0,1), area 7.8mm2, adj f1,f2,f5,f7,f9,f15,f23,f24
  f397: cylinder r=13mm len=3.3mm, axis (0,0,1), area 7.8mm2, adj f1,f3,f5,f10,f12,f14,f21,f22
  f398: cylinder r=13mm len=3.3mm, axis (0,0,1), area 7.8mm2, adj f4,f8,f9,f11,f16,f19,f20,f41
  f399: cylinder r=13mm len=3.3mm, axis (0,0,1), area 7.8mm2, adj f4,f6,f8,f10,f13,f17,f18,f34
PART B: 3 faces, bbox 18.6x18.6x68.9 mm
  f0: cylinder r=9.3mm len=68.9mm, axis (0,0,-1), area 4026.1mm2, adj f1,f2
  f1: plane 18.6x18.6mm, normal (0,0,1), area 271.7mm2, adj f0
  f2: plane 18.6x18.6mm, normal (0,0,-1), area 271.7mm2, adj f0
PLACE A rot(axis=(0,0,1),90deg) t=(-3.26,8.29,30.48)mm
PLACE B t=(-14.56,8.14,-3.07)mm
MATE parallel A.f5 <-> B.f0  axis (0,0,1) through (-15.39,8.29,-6.37)mm
